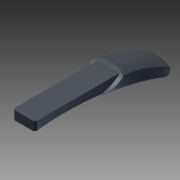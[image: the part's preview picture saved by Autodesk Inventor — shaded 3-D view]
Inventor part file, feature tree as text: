
AUTODESK INVENTOR PART (.ipt)
format: ipt  version: 2011 (Build 150239000, 239)  size: 949,248 bytes
history: native  units: mm (DEFAULTED — no unit token found)
features: sketch x11, plane x8, extrude x8, other x5, fillet x5, rib x2, pattern_linear x2, mirror x2, sweep x1, imported_body x1
ambient origin geometry x8: Origin, YZ Plane, XZ Plane, XY Plane, X Axis, Y Axis, Z Axis, Center Point
bodies: Solid1 (feature_tree)
feature tree (45):
  other  "Upper - Master.ipt"
  plane  "Work Plane1"
  plane  "Work Plane3"
  plane  "Work Plane4"
  plane  "Work Plane5"
  other  "Side Cut"
  extrude  "Extrusion5"  Depth=12.7mm
  extrude  "Extrusion6"  Depth=25.4mm
  extrude  "Extrusion7"  Depth=25.4mm TaperAngle=0.0deg
  extrude  "Extrusion9"  Depth=25.4mm TaperAngle=0.0deg
  fillet  "Fillet11"  Radius=25.4mm
  plane  "Work Plane6"
  sweep  "Sweep1"
  fillet  "Fillet13"  Radius=2.3876mm
  fillet  "Fillet14"  Radius=22.352mm
  fillet  "Fillet15"  Radius=25.4mm
  plane  "Work Plane7"
  rib  "Rib1"
  pattern_linear  "Rectangular Pattern1"  Spacing1=-12.7mm  [1 undecoded]
  mirror  "Mirror1"
  plane  "Work Plane9"
  rib  "Rib2"
  pattern_linear  "Rectangular Pattern2"  Spacing1=2.54mm  [1 undecoded]
  mirror  "Mirror2"
  extrude  "Extrusion10"  Depth=0.762mm
  plane  "Work Plane10"
  extrude  "Extrusion13"  Depth=150.0mm
  extrude  "Extrusion11"  Depth=1.524mm
  extrude  "Extrusion12"  Depth=1.524mm
  fillet  "Fillet17"  Radius=3.175mm
  other  "Slice"
  other  "Work Axis1"
  other  "Srf1"
  sketch  "Sketch8"  dims[d1=10.0mm d23=12.7mm d24=-12.7mm d25=25.4mm d26=-25.4mm]
  sketch  "Sketch9"  dims[d27=6.35mm d28=25.4mm]
  sketch  "Sketch11"  dims[d29=25.4mm d30=0.0mm d31=25.4mm d32=0.0mm]
  sketch  "Sketch13"  dims[d33=19.05mm d34=25.4mm d35=0.0mm d41=25.4mm d42=0.0mm]
  sketch  "Sketch14"  dims[d49=3.175mm d50=-1.524mm d51=2.3876mm d52=22.352mm d53=25.4mm]
  sketch  "Sketch15"  dims[d54=0.0mm]
  sketch  "Sketch16"  dims[d56=3.175mm]
  sketch  "Sketch17"  dims[d58=2.3876mm]
  sketch  "Sketch18"  dims[d59=1.524mm]
  sketch  "Sketch19"  dims[d60=25.4mm]
  sketch  "Sketch21"  dims[d61=1.524mm d62=-12.7mm d63=2.54mm d64=0.762mm d66=150.0mm d68=1.524mm d69=1.524mm d70=3.175mm d71=6.35mm d72=-95.25mm d73=6.35mm d74=6.35mm d75=1.524mm d76=6.35mm d77=2.54mm d78=0.762mm d79=6.35mm d80=40.0mm d82=6.35mm d83=13.4874mm d84=38.1mm d85=6.35mm d86=25.4mm d87=0.0mm d88=4.7752mm d89=6.35mm d90=0.0mm d91=6.35mm d92=0.0mm d93=50.8mm d94=25.4mm d95=11.8872mm d96=0.0mm d98=1.5748mm]
  imported_body  "DerivedBody::Upper - Master.ipt"
note: 2 required parameter values undecoded (feature->parameter linkage not recoverable at this tier; creation-order binding heuristic only, values carry confidence <= 0.55)
